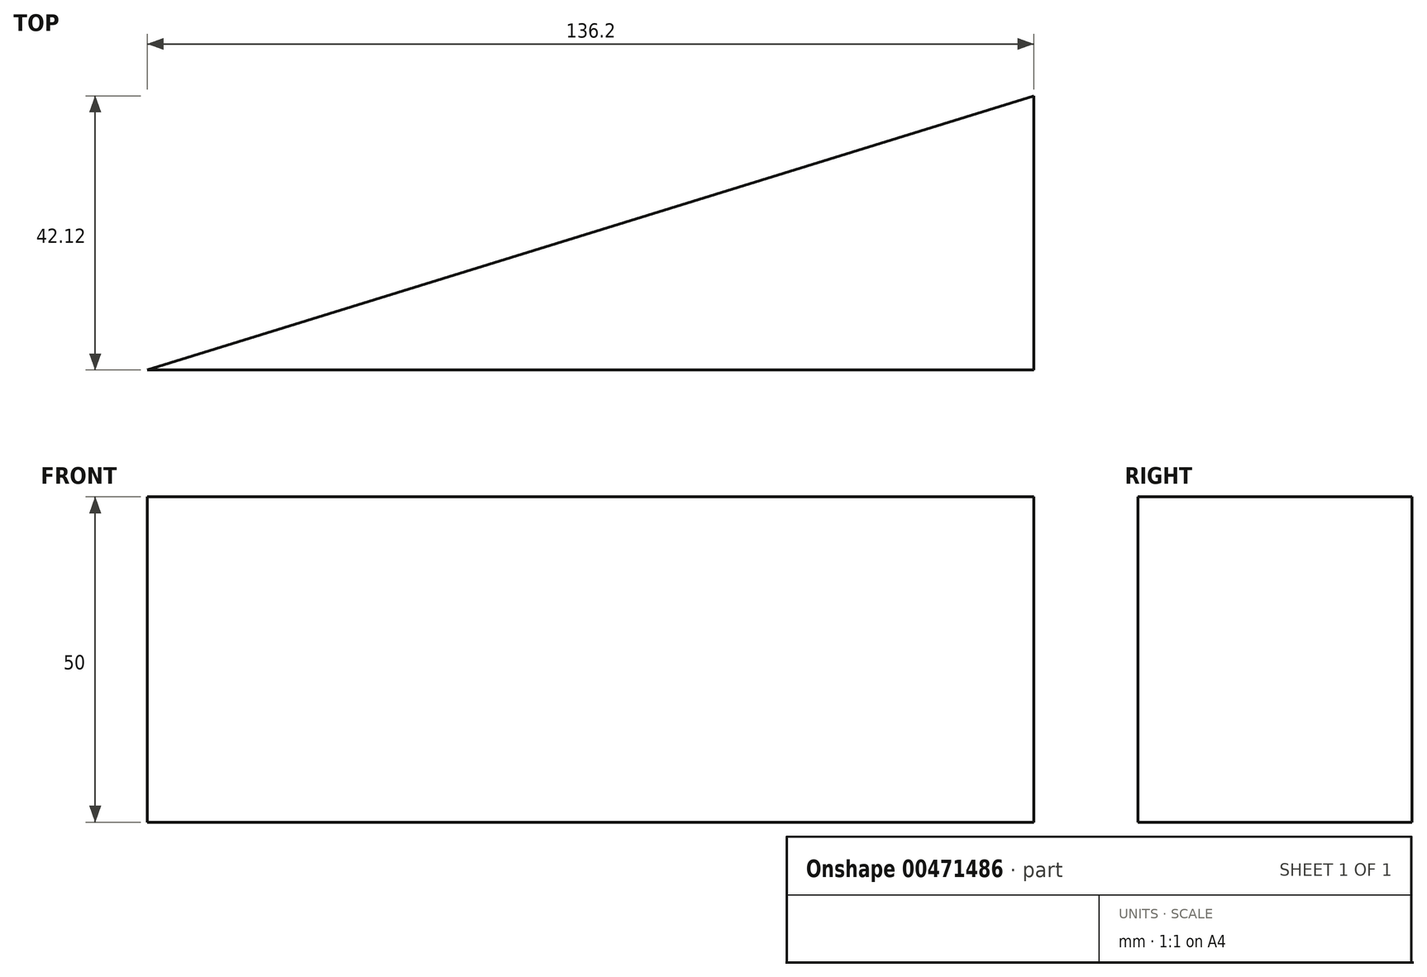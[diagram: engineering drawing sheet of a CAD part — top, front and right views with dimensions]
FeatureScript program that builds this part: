
annotation { "Feature Type Name" : "Feature", "Feature Type Description" : "" }
export const myFeature = defineFeature(function(context is Context, id is Id, definition is map)
    precondition{}
    {
        {
            var Q0;
            Q0=qCreatedBy(makeId("Top.planeOp"),FACE);
            var sketch = newSketch(context, id + "F0", { "sketchPlane" : qUnion([Q0])});
            skLineSegment(sketch, "E0", {"start": v(0, 0) * mm, "end": v(136.2, 42.12) * mm});
            skLineSegment(sketch, "E1", {"start": v(136.2, 42.12) * mm, "end": v(136.2, 0) * mm});
            skLineSegment(sketch, "E2", {"start": v(136.2, 0) * mm, "end": v(0, 0) * mm});
            skSolve(sketch);
        }
        {
            var Q0;
            Q0 = qSketchRegion(id + "F0", true);
            extrude(context, id + "F1", {"entities" : qUnion([Q0]), "depth" : 50 * mm});
        }
    });
